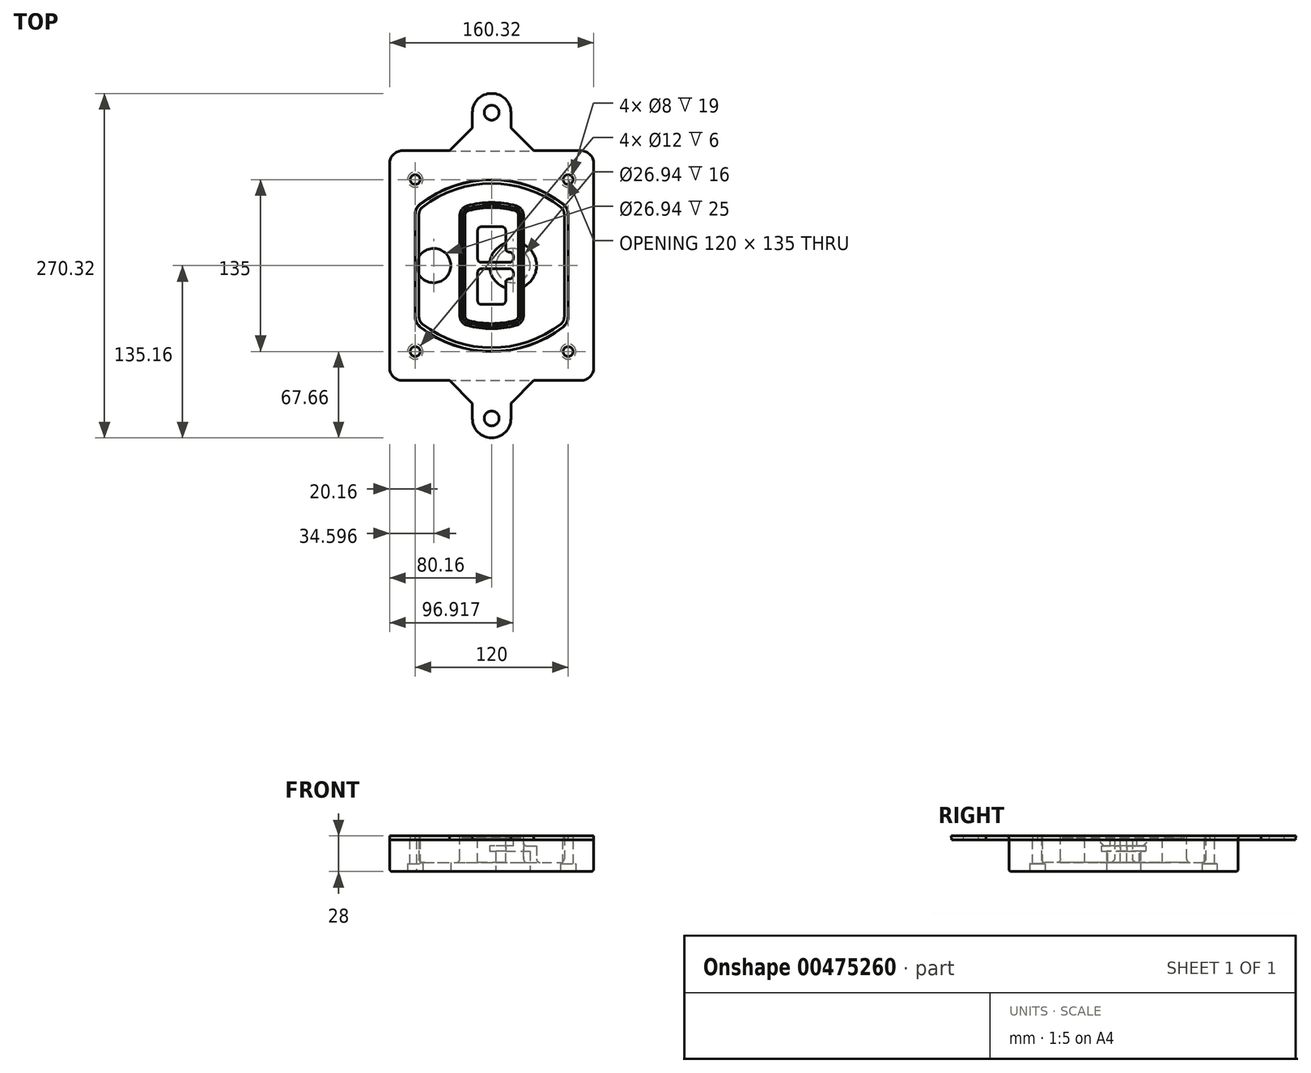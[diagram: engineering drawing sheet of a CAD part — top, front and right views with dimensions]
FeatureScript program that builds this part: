
annotation { "Feature Type Name" : "Feature", "Feature Type Description" : "" }
export const myFeature = defineFeature(function(context is Context, id is Id, definition is map)
    precondition{}
    {
        {
            var Q0;
            Q0=qCreatedBy(makeId("Top.planeOp"),FACE);
            var sketch = newSketch(context, id + "F0", { "sketchPlane" : qUnion([Q0])});
            skPoint(sketch, "E0.rect.middle", {"position": v(0, 0) * mm});
            skLineSegment(sketch, "E1.bottom", {"start": v(-70, -90) * mm, "end": v(70, -90) * mm});
            skLineSegment(sketch, "E1.top", {"start": v(-70, 90) * mm, "end": v(70, 90) * mm});
            skLineSegment(sketch, "E1.left", {"start": v(-80, -80) * mm, "end": v(-80, 80) * mm});
            skLineSegment(sketch, "E1.right", {"start": v(80, -80) * mm, "end": v(80, 80) * mm});
            skLineSegment(sketch, "E2", {"start": v(-80, 90) * mm, "end": v(80, -90) * mm, "construction": true});
            skLineSegment(sketch, "E3", {"start": v(80, 90) * mm, "end": v(-80, -90) * mm, "construction": true});
            skCircle(sketch, "E4", {"center": v(-60, 67.5) * mm, "radius": 4 * mm});
            skCircle(sketch, "E5", {"center": v(60, 67.5) * mm, "radius": 4 * mm});
            skCircle(sketch, "E6", {"center": v(60, -67.5) * mm, "radius": 4 * mm});
            skCircle(sketch, "E7", {"center": v(-60, -67.5) * mm, "radius": 4 * mm});
            skLineSegment(sketch, "E8", {"start": v(-60, 67.5) * mm, "end": v(60, 67.5) * mm, "construction": true});
            skLineSegment(sketch, "E9", {"start": v(60, 67.5) * mm, "end": v(60, -67.5) * mm, "construction": true});
            skLineSegment(sketch, "E10", {"start": v(60, -67.5) * mm, "end": v(-60, -67.5) * mm, "construction": true});
            skLineSegment(sketch, "E11", {"start": v(-60, -67.5) * mm, "end": v(-60, 67.5) * mm, "construction": true});
            skLineSegment(sketch, "E12", {"start": v(-60, 40.3) * mm, "end": v(-60, -40.3) * mm});
            skLineSegment(sketch, "E13", {"start": v(60, 40.3) * mm, "end": v(60, -40.3) * mm});
            skArc(sketch, "E14", {"start": v(56.15, 48.18) * mm, "mid": v(0, 67.5) * mm, "end": v(-56.15, 48.18) * mm});
            skArc(sketch, "E15", {"start": v(-56.15, -48.18) * mm, "mid": v(0, -67.5) * mm, "end": v(56.15, -48.18) * mm});
            skLineSegment(sketch, "E16", {"start": v(-60, 0) * mm, "end": v(60, 0) * mm, "construction": true});
            skPoint(sketch, "E17.visualSharp", {"position": v(-60, -45) * mm});
            skArc(sketch, "E17.filletArc", {"start": v(-60, -40.3) * mm, "mid": v(-58.99, -44.68) * mm, "end": v(-56.15, -48.18) * mm});
            skPoint(sketch, "E18.visualSharp", {"position": v(-60, 45) * mm});
            skArc(sketch, "E18.filletArc", {"start": v(-56.15, 48.18) * mm, "mid": v(-58.99, 44.68) * mm, "end": v(-60, 40.3) * mm});
            skPoint(sketch, "E19.visualSharp", {"position": v(60, 45) * mm});
            skArc(sketch, "E19.filletArc", {"start": v(60, 40.3) * mm, "mid": v(58.99, 44.68) * mm, "end": v(56.15, 48.18) * mm});
            skPoint(sketch, "E20.visualSharp", {"position": v(60, -45) * mm});
            skArc(sketch, "E20.filletArc", {"start": v(56.15, -48.18) * mm, "mid": v(58.99, -44.68) * mm, "end": v(60, -40.3) * mm});
            skPoint(sketch, "E21.visualSharp", {"position": v(-80, 90) * mm});
            skArc(sketch, "E21.filletArc", {"start": v(-70, 90) * mm, "mid": v(-77.07, 87.07) * mm, "end": v(-80, 80) * mm});
            skPoint(sketch, "E22.visualSharp", {"position": v(80, 90) * mm});
            skArc(sketch, "E22.filletArc", {"start": v(80, 80) * mm, "mid": v(77.07, 87.07) * mm, "end": v(70, 90) * mm});
            skPoint(sketch, "E23.visualSharp", {"position": v(80, -90) * mm});
            skArc(sketch, "E23.filletArc", {"start": v(70, -90) * mm, "mid": v(77.07, -87.07) * mm, "end": v(80, -80) * mm});
            skPoint(sketch, "E24.visualSharp", {"position": v(-80, -90) * mm});
            skArc(sketch, "E24.filletArc", {"start": v(-80, -80) * mm, "mid": v(-77.07, -87.07) * mm, "end": v(-70, -90) * mm});
            skArc(sketch, "E25.0", {"start": v(57, 40.3) * mm, "mid": v(56.3, 43.36) * mm, "end": v(54.3, 45.81) * mm});
            skLineSegment(sketch, "E25.1", {"start": v(57, 40.3) * mm, "end": v(57, -40.3) * mm});
            skArc(sketch, "E25.2", {"start": v(54.3, -45.81) * mm, "mid": v(56.3, -43.36) * mm, "end": v(57, -40.3) * mm});
            skArc(sketch, "E25.3", {"start": v(-54.3, -45.81) * mm, "mid": v(0, -64.5) * mm, "end": v(54.3, -45.81) * mm});
            skArc(sketch, "E25.4", {"start": v(-57, -40.3) * mm, "mid": v(-56.3, -43.36) * mm, "end": v(-54.3, -45.81) * mm});
            skArc(sketch, "E25.5", {"start": v(54.3, 45.81) * mm, "mid": v(0, 64.5) * mm, "end": v(-54.3, 45.81) * mm});
            skLineSegment(sketch, "E25.6", {"start": v(-57, 40.3) * mm, "end": v(-57, -40.3) * mm});
            skArc(sketch, "E25.7", {"start": v(-54.3, 45.81) * mm, "mid": v(-56.3, 43.36) * mm, "end": v(-57, 40.3) * mm});
            skArc(sketch, "E26.0", {"start": v(-58.62, 51.33) * mm, "mid": v(-62.58, 46.43) * mm, "end": v(-64, 40.3) * mm});
            skArc(sketch, "E26.1", {"start": v(58.62, 51.33) * mm, "mid": v(0, 71.5) * mm, "end": v(-58.62, 51.33) * mm});
            skArc(sketch, "E26.2", {"start": v(64, 40.3) * mm, "mid": v(62.58, 46.43) * mm, "end": v(58.62, 51.33) * mm});
            skLineSegment(sketch, "E26.3", {"start": v(64, 40.3) * mm, "end": v(64, -40.3) * mm});
            skArc(sketch, "E26.4", {"start": v(58.62, -51.33) * mm, "mid": v(62.58, -46.43) * mm, "end": v(64, -40.3) * mm});
            skLineSegment(sketch, "E26.5", {"start": v(-64, 40.3) * mm, "end": v(-64, -40.3) * mm});
            skArc(sketch, "E26.6", {"start": v(-58.62, -51.33) * mm, "mid": v(0, -71.5) * mm, "end": v(58.62, -51.33) * mm});
            skArc(sketch, "E26.7", {"start": v(-64, -40.3) * mm, "mid": v(-62.58, -46.43) * mm, "end": v(-58.62, -51.33) * mm});
            skSolve(sketch);
        }
        {
            var Q0;
            Q0=makeQuery(id+"F0.imprint","IMPRINT",FACE,{"disambiguationData":[TD([[makeQuery(id+"F0.imprint","IMPRINT",EDGE,{"derivedFrom":sQuery(id+"F0.wireOp",EDGE,"E1.bottom")}),1.0]])]});
            var Q1;
            Q1=makeQuery(id+"F0.imprint","IMPRINT",FACE,{"disambiguationData":[TD([[makeQuery(id+"F0.imprint","IMPRINT",EDGE,{"derivedFrom":sQuery(id+"F0.wireOp",EDGE,"E12")}),1.0]])]});
            var Q2;
            Q2=makeQuery(id+"F0.imprint","IMPRINT",FACE,{"disambiguationData":[TD([[makeQuery(id+"F0.imprint","IMPRINT",EDGE,{"derivedFrom":sQuery(id+"F0.wireOp",EDGE,"E25.0")}),1.0]])]});
            var Q3;
            Q3=makeQuery(id+"F0.imprint","IMPRINT",FACE,{"disambiguationData":[TD([[makeQuery(id+"F0.imprint","IMPRINT",EDGE,{"derivedFrom":sQuery(id+"F0.wireOp",EDGE,"E12")}),-1.0]])]});
            extrude(context, id + "F1", {"entities" : qUnion([Q0, Q1, Q2, Q3]), "oppositeDirection" : true, "depth" : 25 * mm});
        }
        {
            var Q0;
            Q0=makeQuery(id+"F0.imprint","IMPRINT",FACE,{"disambiguationData":[TD([[makeQuery(id+"F0.imprint","IMPRINT",EDGE,{"derivedFrom":sQuery(id+"F0.wireOp",EDGE,"E12")}),1.0]])]});
            extrude(context, id + "F2", {"entities" : qUnion([Q0]), "operationType" : NewBodyOperationType.ADD, "depth" : 3 * mm});
        }
        {
            var Q0;
            Q0=makeQuery(id+"F0.imprint","IMPRINT",FACE,{"disambiguationData":[TD([[makeQuery(id+"F0.imprint","IMPRINT",EDGE,{"derivedFrom":sQuery(id+"F0.wireOp",EDGE,"E25.0")}),1.0]])]});
            extrude(context, id + "F3", {"entities" : qUnion([Q0]), "operationType" : NewBodyOperationType.REMOVE, "oppositeDirection" : true, "depth" : 18 * mm});
        }
        {
            var Q0;
            Q0=makeQuery(id+"F2.opExtrude","CAP_FACE",FACE,{"disambiguationData":[OSD([sQuery(id+"F0.wireOp",EDGE,"E12"),sQuery(id+"F0.wireOp",EDGE,"E13"),sQuery(id+"F0.wireOp",EDGE,"E14"),sQuery(id+"F0.wireOp",EDGE,"E15"),sQuery(id+"F0.wireOp",EDGE,"E17.filletArc"),sQuery(id+"F0.wireOp",EDGE,"E18.filletArc"),sQuery(id+"F0.wireOp",EDGE,"E19.filletArc"),sQuery(id+"F0.wireOp",EDGE,"E20.filletArc"),sQuery(id+"F0.wireOp",EDGE,"E25.0"),sQuery(id+"F0.wireOp",EDGE,"E25.1"),sQuery(id+"F0.wireOp",EDGE,"E25.2"),sQuery(id+"F0.wireOp",EDGE,"E25.3"),sQuery(id+"F0.wireOp",EDGE,"E25.4"),sQuery(id+"F0.wireOp",EDGE,"E25.5"),sQuery(id+"F0.wireOp",EDGE,"E25.6"),sQuery(id+"F0.wireOp",EDGE,"E25.7")])],"isStart":false});
            var sketch = newSketch(context, id + "F4", { "sketchPlane" : qUnion([Q0])});
            skArc(sketch, "E27.0", {"start": v(-19.08, -46.97) * mm, "mid": v(0, -49.5) * mm, "end": v(19.08, -46.97) * mm});
            skArc(sketch, "E28.0", {"start": v(19.08, 46.97) * mm, "mid": v(0, 49.5) * mm, "end": v(-19.08, 46.97) * mm});
            skLineSegment(sketch, "E29", {"start": v(-25, 39.25) * mm, "end": v(-25, -39.25) * mm});
            skLineSegment(sketch, "E30", {"start": v(25, 39.25) * mm, "end": v(25, -39.25) * mm});
            skLineSegment(sketch, "E31", {"start": v(-25, 45.1) * mm, "end": v(25, 45.1) * mm, "construction": true});
            skLineSegment(sketch, "E32", {"start": v(-25, -45.1) * mm, "end": v(25, -45.1) * mm, "construction": true});
            skPoint(sketch, "E33.visualSharp", {"position": v(-25, 45.1) * mm});
            skArc(sketch, "E33.filletArc", {"start": v(-19.08, 46.97) * mm, "mid": v(-23.35, 44.11) * mm, "end": v(-25, 39.25) * mm});
            skPoint(sketch, "E34.visualSharp", {"position": v(25, 45.1) * mm});
            skArc(sketch, "E34.filletArc", {"start": v(25, 39.25) * mm, "mid": v(23.35, 44.11) * mm, "end": v(19.08, 46.97) * mm});
            skPoint(sketch, "E35.visualSharp", {"position": v(25, -45.1) * mm});
            skArc(sketch, "E35.filletArc", {"start": v(19.08, -46.97) * mm, "mid": v(23.35, -44.11) * mm, "end": v(25, -39.25) * mm});
            skPoint(sketch, "E36.visualSharp", {"position": v(-25, -45.1) * mm});
            skArc(sketch, "E36.filletArc", {"start": v(-25, -39.25) * mm, "mid": v(-23.35, -44.11) * mm, "end": v(-19.08, -46.97) * mm});
            skArc(sketch, "E37.0", {"start": v(54.3, 45.81) * mm, "mid": v(0, 64.5) * mm, "end": v(-54.3, 45.81) * mm});
            skArc(sketch, "E37.1", {"start": v(-54.3, 45.81) * mm, "mid": v(-56.3, 43.36) * mm, "end": v(-57, 40.3) * mm});
            skLineSegment(sketch, "E37.2", {"start": v(-57, 40.3) * mm, "end": v(-57, -40.3) * mm});
            skArc(sketch, "E37.3", {"start": v(-57, -40.3) * mm, "mid": v(-56.3, -43.36) * mm, "end": v(-54.3, -45.81) * mm});
            skArc(sketch, "E37.4", {"start": v(-54.3, -45.81) * mm, "mid": v(0, -64.5) * mm, "end": v(54.3, -45.81) * mm});
            skArc(sketch, "E37.5", {"start": v(54.3, -45.81) * mm, "mid": v(56.3, -43.36) * mm, "end": v(57, -40.3) * mm});
            skLineSegment(sketch, "E37.6", {"start": v(57, 40.3) * mm, "end": v(57, -40.3) * mm});
            skArc(sketch, "E37.7", {"start": v(57, 40.3) * mm, "mid": v(56.3, 43.36) * mm, "end": v(54.3, 45.81) * mm});
            skLineSegment(sketch, "E38.0", {"start": v(23, 39.25) * mm, "end": v(23, -39.25) * mm});
            skArc(sketch, "E38.1", {"start": v(18.56, -45.04) * mm, "mid": v(21.76, -42.9) * mm, "end": v(23, -39.25) * mm});
            skArc(sketch, "E38.2", {"start": v(-18.56, -45.04) * mm, "mid": v(0, -47.5) * mm, "end": v(18.56, -45.04) * mm});
            skArc(sketch, "E38.3", {"start": v(-23, -39.25) * mm, "mid": v(-21.76, -42.9) * mm, "end": v(-18.56, -45.04) * mm});
            skLineSegment(sketch, "E38.4", {"start": v(-23, 39.25) * mm, "end": v(-23, -39.25) * mm});
            skArc(sketch, "E38.5", {"start": v(23, 39.25) * mm, "mid": v(21.76, 42.9) * mm, "end": v(18.56, 45.04) * mm});
            skArc(sketch, "E38.6", {"start": v(-18.56, 45.04) * mm, "mid": v(-21.76, 42.9) * mm, "end": v(-23, 39.25) * mm});
            skArc(sketch, "E38.7", {"start": v(18.56, 45.04) * mm, "mid": v(0, 47.5) * mm, "end": v(-18.56, 45.04) * mm});
            skArc(sketch, "E39.0", {"start": v(21, 39.25) * mm, "mid": v(20.18, 41.68) * mm, "end": v(18.04, 43.1) * mm});
            skLineSegment(sketch, "E39.1", {"start": v(21, 39.25) * mm, "end": v(21, -39.25) * mm});
            skArc(sketch, "E39.2", {"start": v(18.04, -43.1) * mm, "mid": v(20.18, -41.68) * mm, "end": v(21, -39.25) * mm});
            skArc(sketch, "E39.3", {"start": v(-18.04, -43.1) * mm, "mid": v(0, -45.5) * mm, "end": v(18.04, -43.1) * mm});
            skArc(sketch, "E39.4", {"start": v(-21, -39.25) * mm, "mid": v(-20.18, -41.68) * mm, "end": v(-18.04, -43.1) * mm});
            skArc(sketch, "E39.5", {"start": v(18.04, 43.1) * mm, "mid": v(0, 45.5) * mm, "end": v(-18.04, 43.1) * mm});
            skLineSegment(sketch, "E39.6", {"start": v(-21, 39.25) * mm, "end": v(-21, -39.25) * mm});
            skArc(sketch, "E39.7", {"start": v(-18.04, 43.1) * mm, "mid": v(-20.18, 41.68) * mm, "end": v(-21, 39.25) * mm});
            skLineSegment(sketch, "E40", {"start": v(-25, 0) * mm, "end": v(25, 0) * mm, "construction": true});
            skLineSegment(sketch, "E41", {"start": v(-11, 5.5) * mm, "end": v(-11, 27.5) * mm});
            skLineSegment(sketch, "E42", {"start": v(-8, 30.5) * mm, "end": v(8, 30.5) * mm});
            skLineSegment(sketch, "E43", {"start": v(11, 27.5) * mm, "end": v(11, 13.5) * mm});
            skLineSegment(sketch, "E44", {"start": v(14, 10.5) * mm, "end": v(14, 10.5) * mm});
            skLineSegment(sketch, "E45", {"start": v(17, 7.5) * mm, "end": v(17, 5.5) * mm});
            skLineSegment(sketch, "E46", {"start": v(14, 2.5) * mm, "end": v(-8, 2.5) * mm});
            skPoint(sketch, "E47.visualSharp", {"position": v(-11, 30.5) * mm});
            skArc(sketch, "E47.filletArc", {"start": v(-8, 30.5) * mm, "mid": v(-10.12, 29.62) * mm, "end": v(-11, 27.5) * mm});
            skPoint(sketch, "E48.visualSharp", {"position": v(11, 30.5) * mm});
            skArc(sketch, "E48.filletArc", {"start": v(11, 27.5) * mm, "mid": v(10.12, 29.62) * mm, "end": v(8, 30.5) * mm});
            skPoint(sketch, "E49.visualSharp", {"position": v(11, 10.5) * mm});
            skArc(sketch, "E49.filletArc", {"start": v(11, 13.5) * mm, "mid": v(11.88, 11.38) * mm, "end": v(14, 10.5) * mm});
            skPoint(sketch, "E50.visualSharp", {"position": v(17, 10.5) * mm});
            skArc(sketch, "E50.filletArc", {"start": v(17, 7.5) * mm, "mid": v(16.12, 9.62) * mm, "end": v(14, 10.5) * mm});
            skPoint(sketch, "E51.visualSharp", {"position": v(17, 2.5) * mm});
            skArc(sketch, "E51.filletArc", {"start": v(14, 2.5) * mm, "mid": v(16.12, 3.38) * mm, "end": v(17, 5.5) * mm});
            skPoint(sketch, "E52.visualSharp", {"position": v(-11, 2.5) * mm});
            skArc(sketch, "E52.filletArc", {"start": v(-11, 5.5) * mm, "mid": v(-10.12, 3.38) * mm, "end": v(-8, 2.5) * mm});
            skLineSegment(sketch, "E53.0.MirrorCS", {"start": v(14, -2.5) * mm, "end": v(-8, -2.5) * mm});
            skArc(sketch, "E54.0.MirrorCS", {"start": v(-11, -5.5) * mm, "mid": v(-10.12, -3.38) * mm, "end": v(-8, -2.5) * mm});
            skLineSegment(sketch, "E55.0.MirrorCS", {"start": v(-11, -5.5) * mm, "end": v(-11, -27.5) * mm});
            skArc(sketch, "E56.0.MirrorCS", {"start": v(-8, -30.5) * mm, "mid": v(-10.12, -29.62) * mm, "end": v(-11, -27.5) * mm});
            skLineSegment(sketch, "E57.0.MirrorCS", {"start": v(-8, -30.5) * mm, "end": v(8, -30.5) * mm});
            skArc(sketch, "E58.0.MirrorCS", {"start": v(11, -27.5) * mm, "mid": v(10.12, -29.62) * mm, "end": v(8, -30.5) * mm});
            skLineSegment(sketch, "E59.0.MirrorCS", {"start": v(11, -27.5) * mm, "end": v(11, -13.5) * mm});
            skArc(sketch, "E60.0.MirrorCS", {"start": v(11, -13.5) * mm, "mid": v(11.88, -11.38) * mm, "end": v(14, -10.5) * mm});
            skArc(sketch, "E61.0.MirrorCS", {"start": v(17, -7.5) * mm, "mid": v(16.12, -9.62) * mm, "end": v(14, -10.5) * mm});
            skLineSegment(sketch, "E62.0.MirrorCS", {"start": v(17, -7.5) * mm, "end": v(17, -5.5) * mm});
            skArc(sketch, "E63.0.MirrorCS", {"start": v(14, -2.5) * mm, "mid": v(16.12, -3.38) * mm, "end": v(17, -5.5) * mm});
            skSolve(sketch);
        }
        {
            var Q0;
            Q0=makeQuery(id+"F4.imprint","IMPRINT",FACE,{"disambiguationData":[TD([[makeQuery(id+"F4.imprint","IMPRINT",EDGE,{"derivedFrom":sQuery(id+"F4.wireOp",EDGE,"E27.0")}),1.0]])]});
            var Q1;
            Q1=makeQuery(id+"F4.imprint","IMPRINT",FACE,{"disambiguationData":[TD([[makeQuery(id+"F4.imprint","IMPRINT",EDGE,{"derivedFrom":sQuery(id+"F4.wireOp",EDGE,"E38.0")}),-1.0]])]});
            var Q2;
            Q2=makeQuery(id+"F4.imprint","IMPRINT",FACE,{"disambiguationData":[TD([[makeQuery(id+"F4.imprint","IMPRINT",EDGE,{"derivedFrom":sQuery(id+"F4.wireOp",EDGE,"E39.0")}),1.0]])]});
            extrude(context, id + "F5", {"entities" : qUnion([Q0, Q1, Q2]), "operationType" : NewBodyOperationType.ADD, "endBound" : BoundingType.UP_TO_NEXT, "oppositeDirection" : true, "depth" : 25 * mm});
        }
        {
            var Q0;
            Q0=makeQuery(id+"F4.imprint","IMPRINT",FACE,{"disambiguationData":[TD([[makeQuery(id+"F4.imprint","IMPRINT",EDGE,{"derivedFrom":sQuery(id+"F4.wireOp",EDGE,"E38.0")}),-1.0]])]});
            extrude(context, id + "F6", {"entities" : qUnion([Q0]), "operationType" : NewBodyOperationType.REMOVE, "oppositeDirection" : true, "depth" : 2 * mm});
        }
        {
            var Q0;
            Q0=makeQuery(id+"F1.opExtrude","CAP_FACE",FACE,{"disambiguationData":[OSD([sQuery(id+"F0.wireOp",EDGE,"E1.bottom"),sQuery(id+"F0.wireOp",EDGE,"E1.top"),sQuery(id+"F0.wireOp",EDGE,"E1.left"),sQuery(id+"F0.wireOp",EDGE,"E1.right"),sQuery(id+"F0.wireOp",EDGE,"E4"),sQuery(id+"F0.wireOp",EDGE,"E5"),sQuery(id+"F0.wireOp",EDGE,"E6"),sQuery(id+"F0.wireOp",EDGE,"E7"),sQuery(id+"F0.wireOp",EDGE,"E21.filletArc"),sQuery(id+"F0.wireOp",EDGE,"E22.filletArc"),sQuery(id+"F0.wireOp",EDGE,"E23.filletArc"),sQuery(id+"F0.wireOp",EDGE,"E24.filletArc")])],"isStart":false});
            var sketch = newSketch(context, id + "F7", { "sketchPlane" : qUnion([Q0])});
            skCircle(sketch, "E64", {"center": v(16.76, 0) * mm, "radius": 13.47 * mm});
            skCircle(sketch, "E65", {"center": v(-45.56, 0) * mm, "radius": 13.47 * mm});
            skLineSegment(sketch, "E66", {"start": v(80, 0) * mm, "end": v(-80, 0) * mm});
            skCircle(sketch, "E67", {"center": v(16.76, 0) * mm, "radius": 18.47 * mm});
            skCircle(sketch, "E68", {"center": v(60, -67.5) * mm, "radius": 6 * mm});
            skCircle(sketch, "E69", {"center": v(-60, -67.5) * mm, "radius": 6 * mm});
            skCircle(sketch, "E70", {"center": v(-60, 67.5) * mm, "radius": 6 * mm});
            skCircle(sketch, "E71", {"center": v(60, 67.5) * mm, "radius": 6 * mm});
            skSolve(sketch);
        }
        {
            var Q0;
            {var subQ1=sQuery(id+"F7.wireOp",EDGE,"E66");var subQ4=sQuery(id+"F7.wireOp",EDGE,"E64");var subQ6=makeQuery(id+"F7.imprint","INTERSECT",VERTEX,{"disambiguationData":[OD(0.0)],"derivedFrom":[subQ4,subQ1]});Q0=makeQuery(id+"F7.imprint","IMPRINT",FACE,{"disambiguationData":[TD([[makeQuery(id+"F7.imprint","IMPRINT",EDGE,{"disambiguationData":[TD([[subQ6,-1.0]])],"derivedFrom":subQ4}),-1.0]])]});}
            var Q1;
            {var subQ0=sQuery(id+"F7.wireOp",EDGE,"E66");var subQ1=sQuery(id+"F7.wireOp",EDGE,"E64");var subQ3=makeQuery(id+"F7.imprint","INTERSECT",VERTEX,{"disambiguationData":[OD(0.0)],"derivedFrom":[subQ1,subQ0]});Q1=makeQuery(id+"F7.imprint","IMPRINT",FACE,{"disambiguationData":[TD([[makeQuery(id+"F7.imprint","IMPRINT",EDGE,{"disambiguationData":[TD([[subQ3,-1.0]])],"derivedFrom":subQ1}),1.0]])]});}
            var Q2;
            {var subQ0=sQuery(id+"F7.wireOp",EDGE,"E66");var subQ1=sQuery(id+"F7.wireOp",EDGE,"E64");var subQ3=makeQuery(id+"F7.imprint","INTERSECT",VERTEX,{"disambiguationData":[OD(0.0)],"derivedFrom":[subQ1,subQ0]});Q2=makeQuery(id+"F7.imprint","IMPRINT",FACE,{"disambiguationData":[TD([[makeQuery(id+"F7.imprint","IMPRINT",EDGE,{"disambiguationData":[TD([[subQ3,1.0]])],"derivedFrom":subQ1}),1.0]])]});}
            var Q3;
            {var subQ1=sQuery(id+"F7.wireOp",EDGE,"E66");var subQ4=sQuery(id+"F7.wireOp",EDGE,"E64");var subQ6=makeQuery(id+"F7.imprint","INTERSECT",VERTEX,{"disambiguationData":[OD(0.0)],"derivedFrom":[subQ4,subQ1]});Q3=makeQuery(id+"F7.imprint","IMPRINT",FACE,{"disambiguationData":[TD([[makeQuery(id+"F7.imprint","IMPRINT",EDGE,{"disambiguationData":[TD([[subQ6,1.0]])],"derivedFrom":subQ4}),-1.0]])]});}
            extrude(context, id + "F8", {"entities" : qUnion([Q0, Q1, Q2, Q3]), "operationType" : NewBodyOperationType.ADD, "oppositeDirection" : true, "depth" : 20 * mm});
        }
        {
            var Q0;
            {var subQ0=sQuery(id+"F7.wireOp",EDGE,"E66");var subQ1=sQuery(id+"F7.wireOp",EDGE,"E64");var subQ3=makeQuery(id+"F7.imprint","INTERSECT",VERTEX,{"disambiguationData":[OD(0.0)],"derivedFrom":[subQ1,subQ0]});Q0=makeQuery(id+"F7.imprint","IMPRINT",FACE,{"disambiguationData":[TD([[makeQuery(id+"F7.imprint","IMPRINT",EDGE,{"disambiguationData":[TD([[subQ3,-1.0]])],"derivedFrom":subQ1}),1.0]])]});}
            var Q1;
            {var subQ0=sQuery(id+"F7.wireOp",EDGE,"E66");var subQ1=sQuery(id+"F7.wireOp",EDGE,"E64");var subQ3=makeQuery(id+"F7.imprint","INTERSECT",VERTEX,{"disambiguationData":[OD(0.0)],"derivedFrom":[subQ1,subQ0]});Q1=makeQuery(id+"F7.imprint","IMPRINT",FACE,{"disambiguationData":[TD([[makeQuery(id+"F7.imprint","IMPRINT",EDGE,{"disambiguationData":[TD([[subQ3,1.0]])],"derivedFrom":subQ1}),1.0]])]});}
            extrude(context, id + "F9", {"entities" : qUnion([Q0, Q1]), "operationType" : NewBodyOperationType.REMOVE, "oppositeDirection" : true, "depth" : 16 * mm});
        }
        {
            var Q0;
            {var subQ0=sQuery(id+"F7.wireOp",EDGE,"E66");var subQ1=sQuery(id+"F7.wireOp",EDGE,"E65");var subQ3=makeQuery(id+"F7.imprint","INTERSECT",VERTEX,{"disambiguationData":[OD(0.0)],"derivedFrom":[subQ1,subQ0]});Q0=makeQuery(id+"F7.imprint","IMPRINT",FACE,{"disambiguationData":[TD([[makeQuery(id+"F7.imprint","IMPRINT",EDGE,{"disambiguationData":[TD([[subQ3,-1.0]])],"derivedFrom":subQ1}),1.0]])]});}
            var Q1;
            {var subQ0=sQuery(id+"F7.wireOp",EDGE,"E66");var subQ1=sQuery(id+"F7.wireOp",EDGE,"E65");var subQ3=makeQuery(id+"F7.imprint","INTERSECT",VERTEX,{"disambiguationData":[OD(0.0)],"derivedFrom":[subQ1,subQ0]});Q1=makeQuery(id+"F7.imprint","IMPRINT",FACE,{"disambiguationData":[TD([[makeQuery(id+"F7.imprint","IMPRINT",EDGE,{"disambiguationData":[TD([[subQ3,1.0]])],"derivedFrom":subQ1}),1.0]])]});}
            extrude(context, id + "F10", {"entities" : qUnion([Q0, Q1]), "operationType" : NewBodyOperationType.REMOVE, "oppositeDirection" : true, "depth" : 25 * mm});
        }
        {
            var Q0;
            Q0=makeQuery(id+"F7.imprint","IMPRINT",FACE,{"disambiguationData":[TD([[makeQuery(id+"F7.imprint","IMPRINT",EDGE,{"derivedFrom":sQuery(id+"F7.wireOp",EDGE,"E68")}),1.0]])]});
            var Q1;
            Q1=makeQuery(id+"F7.imprint","IMPRINT",FACE,{"disambiguationData":[TD([[makeQuery(id+"F7.imprint","IMPRINT",EDGE,{"derivedFrom":makeQuery(id+"F1.opExtrude","CAP_EDGE",EDGE,{"disambiguationData":[OSD([sQuery(id+"F0.wireOp",EDGE,"E5")])],"isStart":false})}),-1.0]])]});
            var Q2;
            Q2=makeQuery(id+"F7.imprint","IMPRINT",FACE,{"disambiguationData":[TD([[makeQuery(id+"F7.imprint","IMPRINT",EDGE,{"derivedFrom":sQuery(id+"F7.wireOp",EDGE,"E69")}),1.0]])]});
            var Q3;
            Q3=makeQuery(id+"F7.imprint","IMPRINT",FACE,{"disambiguationData":[TD([[makeQuery(id+"F7.imprint","IMPRINT",EDGE,{"derivedFrom":makeQuery(id+"F1.opExtrude","CAP_EDGE",EDGE,{"disambiguationData":[OSD([sQuery(id+"F0.wireOp",EDGE,"E4")])],"isStart":false})}),-1.0]])]});
            var Q4;
            Q4=makeQuery(id+"F7.imprint","IMPRINT",FACE,{"disambiguationData":[TD([[makeQuery(id+"F7.imprint","IMPRINT",EDGE,{"derivedFrom":sQuery(id+"F7.wireOp",EDGE,"E70")}),1.0]])]});
            var Q5;
            Q5=makeQuery(id+"F7.imprint","IMPRINT",FACE,{"disambiguationData":[TD([[makeQuery(id+"F7.imprint","IMPRINT",EDGE,{"derivedFrom":makeQuery(id+"F1.opExtrude","CAP_EDGE",EDGE,{"disambiguationData":[OSD([sQuery(id+"F0.wireOp",EDGE,"E7")])],"isStart":false})}),-1.0]])]});
            var Q6;
            Q6=makeQuery(id+"F7.imprint","IMPRINT",FACE,{"disambiguationData":[TD([[makeQuery(id+"F7.imprint","IMPRINT",EDGE,{"derivedFrom":sQuery(id+"F7.wireOp",EDGE,"E71")}),1.0]])]});
            var Q7;
            Q7=makeQuery(id+"F7.imprint","IMPRINT",FACE,{"disambiguationData":[TD([[makeQuery(id+"F7.imprint","IMPRINT",EDGE,{"derivedFrom":makeQuery(id+"F1.opExtrude","CAP_EDGE",EDGE,{"disambiguationData":[OSD([sQuery(id+"F0.wireOp",EDGE,"E6")])],"isStart":false})}),-1.0]])]});
            extrude(context, id + "F11", {"entities" : qUnion([Q0, Q1, Q2, Q3, Q4, Q5, Q6, Q7]), "operationType" : NewBodyOperationType.REMOVE, "oppositeDirection" : true, "depth" : 6 * mm});
        }
        {
            var Q0;
            Q0=makeQuery(id+"F9.boolean.opBoolean","COPY",FACE,{"derivedFrom":makeQuery(id+"F9.opExtrude","CAP_FACE",FACE,{"disambiguationData":[OSD([sQuery(id+"F7.wireOp",EDGE,"E64")])],"isStart":false})});
            var sketch = newSketch(context, id + "F12", { "sketchPlane" : qUnion([Q0])});
            skArc(sketch, "E72.0", {"start": v(11, 17.55) * mm, "mid": v(2.57, 11.82) * mm, "end": v(-1.54, 2.5) * mm});
            skArc(sketch, "E72.1", {"start": v(-1.54, -2.5) * mm, "mid": v(2.57, -11.82) * mm, "end": v(11, -17.55) * mm});
            skLineSegment(sketch, "E73", {"start": v(-1.54, -2.5) * mm, "end": v(14, -2.5) * mm});
            skLineSegment(sketch, "E74.0", {"start": v(14, 2.5) * mm, "end": v(-1.54, 2.5) * mm});
            skArc(sketch, "E74.1", {"start": v(14, 2.5) * mm, "mid": v(16.12, 3.38) * mm, "end": v(17, 5.5) * mm});
            skLineSegment(sketch, "E74.2", {"start": v(17, 7.5) * mm, "end": v(17, 5.5) * mm});
            skArc(sketch, "E74.3", {"start": v(17, 7.5) * mm, "mid": v(16.12, 9.62) * mm, "end": v(14, 10.5) * mm});
            skArc(sketch, "E74.4", {"start": v(11, 13.5) * mm, "mid": v(11.88, 11.38) * mm, "end": v(14, 10.5) * mm});
            skLineSegment(sketch, "E74.5", {"start": v(11, 17.55) * mm, "end": v(11, 13.5) * mm});
            skLineSegment(sketch, "E74.7", {"start": v(14, -2.5) * mm, "end": v(-1.54, -2.5) * mm});
            skArc(sketch, "E74.8", {"start": v(14, -2.5) * mm, "mid": v(16.12, -3.38) * mm, "end": v(17, -5.5) * mm});
            skLineSegment(sketch, "E74.9", {"start": v(17, -7.5) * mm, "end": v(17, -5.5) * mm});
            skArc(sketch, "E74.10", {"start": v(17, -7.5) * mm, "mid": v(16.12, -9.62) * mm, "end": v(14, -10.5) * mm});
            skArc(sketch, "E74.11", {"start": v(11, -13.5) * mm, "mid": v(11.88, -11.38) * mm, "end": v(14, -10.5) * mm});
            skLineSegment(sketch, "E74.12", {"start": v(11, -17.55) * mm, "end": v(11, -13.5) * mm});
            skPoint(sketch, "E75.orphan", {"position": v(11, -27.5) * mm});
            skPoint(sketch, "E76.orphan", {"position": v(-8, -2.5) * mm});
            skPoint(sketch, "E77.orphan", {"position": v(-8, 2.5) * mm});
            skPoint(sketch, "E78.orphan", {"position": v(11, 27.5) * mm});
            skSolve(sketch);
        }
        {
            var Q0;
            {var subQ7=sQuery(id+"F12.wireOp",EDGE,"E72.0");var subQ14=sQuery(id+"F12.wireOp",EDGE,"E72.1");var subQ16=sQuery(id+"F12.wireOp",EDGE,"E74.1");var subQ18=sQuery(id+"F12.wireOp",EDGE,"E74.8");Q0=qUnion([makeQuery(id+"F12.imprint","IMPRINT",FACE,{"disambiguationData":[TD([[makeQuery(id+"F12.imprint","IMPRINT",EDGE,{"derivedFrom":subQ7}),1.0]])]}),makeQuery(id+"F12.imprint","IMPRINT",FACE,{"disambiguationData":[TD([[makeQuery(id+"F12.imprint","IMPRINT",EDGE,{"derivedFrom":subQ14}),1.0]])]}),makeQuery(id+"F12.imprint","IMPRINT",FACE,{"disambiguationData":[TD([[makeQuery(id+"F12.imprint","IMPRINT",EDGE,{"derivedFrom":subQ16}),1.0]])]}),makeQuery(id+"F12.imprint","IMPRINT",FACE,{"disambiguationData":[TD([[makeQuery(id+"F12.imprint","IMPRINT",EDGE,{"derivedFrom":subQ18}),-1.0]])]})]);}
            var Q1;
            Q1=makeQuery(id+"F5.boolean.opBoolean","SPLIT",FACE,{"disambiguationData":[TD([makeQuery(id+"F5.opExtrude","SWEPT_FACE",FACE,{"disambiguationData":[OSD([sQuery(id+"F4.wireOp",EDGE,"E41")])]})])],"derivedFrom":makeQuery(id+"F3.boolean.opBoolean","COPY",FACE,{"derivedFrom":makeQuery(id+"F3.opExtrude","CAP_FACE",FACE,{"disambiguationData":[OSD([sQuery(id+"F0.wireOp",EDGE,"E25.0"),sQuery(id+"F0.wireOp",EDGE,"E25.1"),sQuery(id+"F0.wireOp",EDGE,"E25.2"),sQuery(id+"F0.wireOp",EDGE,"E25.3"),sQuery(id+"F0.wireOp",EDGE,"E25.4"),sQuery(id+"F0.wireOp",EDGE,"E25.5"),sQuery(id+"F0.wireOp",EDGE,"E25.6"),sQuery(id+"F0.wireOp",EDGE,"E25.7")])],"isStart":false})})});
            extrude(context, id + "F13", {"entities" : qUnion([Q0]), "operationType" : NewBodyOperationType.REMOVE, "endBound" : BoundingType.UP_TO_SURFACE, "endBoundEntityFace" : qUnion([Q1]), "depth" : 25 * mm});
        }
        {
            var Q0;
            Q0=makeQuery(id+"F3.boolean.opBoolean","COPY",EDGE,{"derivedFrom":makeQuery(id+"F3.opExtrude","CAP_EDGE",EDGE,{"disambiguationData":[OSD([sQuery(id+"F0.wireOp",EDGE,"E25.6")])],"isStart":false})});
            var Q1;
            Q1=makeQuery(id+"F8.boolean.opBoolean","INTERSECT",EDGE,{"derivedFrom":[makeQuery(id+"F5.opExtrude","SWEPT_FACE",FACE,{"disambiguationData":[OSD([sQuery(id+"F4.wireOp",EDGE,"E30")])]}),makeQuery(id+"F8.opExtrude","CAP_FACE",FACE,{"disambiguationData":[OSD([sQuery(id+"F7.wireOp",EDGE,"E67")])],"isStart":false})]});
            var Q2;
            Q2=makeQuery(id+"F8.boolean.opBoolean","INTERSECT",EDGE,{"disambiguationData":[OD(1.0)],"derivedFrom":[makeQuery(id+"F5.opExtrude","SWEPT_FACE",FACE,{"disambiguationData":[OSD([sQuery(id+"F4.wireOp",EDGE,"E30")])]}),makeQuery(id+"F8.opExtrude","SWEPT_FACE",FACE,{"disambiguationData":[OSD([sQuery(id+"F7.wireOp",EDGE,"E67")])]})]});
            var Q3;
            {var subQ0=sQuery(id+"F4.wireOp",EDGE,"E30");Q3=makeQuery(id+"F8.boolean.opBoolean","SPLIT",EDGE,{"disambiguationData":[TD([makeQuery(id+"F5.opExtrude","SWEPT_FACE",FACE,{"disambiguationData":[OSD([sQuery(id+"F4.wireOp",EDGE,"E35.filletArc")])]})])],"derivedFrom":makeQuery(id+"F5.opExtrude","CAP_EDGE",EDGE,{"disambiguationData":[OSD([subQ0])],"isStart":false})});}
            var Q4;
            {var subQ0=sQuery(id+"F0.wireOp",EDGE,"E25.7");var subQ1=sQuery(id+"F0.wireOp",EDGE,"E25.1");var subQ2=sQuery(id+"F0.wireOp",EDGE,"E25.6");var subQ3=sQuery(id+"F0.wireOp",EDGE,"E25.5");var subQ4=sQuery(id+"F0.wireOp",EDGE,"E25.4");var subQ5=sQuery(id+"F0.wireOp",EDGE,"E25.0");var subQ6=sQuery(id+"F0.wireOp",EDGE,"E25.2");var subQ7=sQuery(id+"F0.wireOp",EDGE,"E25.3");Q4=makeQuery(id+"F8.boolean.opBoolean","INTERSECT",EDGE,{"derivedFrom":[makeQuery(id+"F5.boolean.opBoolean","SPLIT",FACE,{"disambiguationData":[TD([makeQuery(id+"F2.opExtrude","SWEPT_FACE",FACE,{"disambiguationData":[OSD([subQ5])]})])],"derivedFrom":makeQuery(id+"F3.boolean.opBoolean","COPY",FACE,{"derivedFrom":makeQuery(id+"F3.opExtrude","CAP_FACE",FACE,{"disambiguationData":[OSD([subQ5,subQ1,subQ6,subQ7,subQ4,subQ3,subQ2,subQ0])],"isStart":false})})}),makeQuery(id+"F8.opExtrude","SWEPT_FACE",FACE,{"disambiguationData":[OSD([sQuery(id+"F7.wireOp",EDGE,"E67")])]})]});}
            var Q5;
            Q5=makeQuery(id+"F8.boolean.opBoolean","INTERSECT",EDGE,{"disambiguationData":[OD(0.0)],"derivedFrom":[makeQuery(id+"F5.opExtrude","SWEPT_FACE",FACE,{"disambiguationData":[OSD([sQuery(id+"F4.wireOp",EDGE,"E30")])]}),makeQuery(id+"F8.opExtrude","SWEPT_FACE",FACE,{"disambiguationData":[OSD([sQuery(id+"F7.wireOp",EDGE,"E67")])]})]});
            fillet(context, id + "F14", {"entities" : qUnion([Q0, Q1, Q2, Q3, Q4, Q5]), "radius" : 3 * mm, "tangentPropagation" : true, "allowEdgeOverflow" : false});
        }
        {
            var Q0;
            Q0=makeQuery(id+"F1.opExtrude","CAP_EDGE",EDGE,{"disambiguationData":[OSD([sQuery(id+"F0.wireOp",EDGE,"E1.bottom")])],"isStart":false});
            fillet(context, id + "F15", {"entities" : qUnion([Q0]), "radius" : 2 * mm, "tangentPropagation" : true, "allowEdgeOverflow" : false});
        }
        {
            var Q0;
            {var subQ0=sQuery(id+"F0.wireOp",EDGE,"E21.filletArc");var subQ1=sQuery(id+"F0.wireOp",EDGE,"E7");var subQ2=sQuery(id+"F0.wireOp",EDGE,"E6");var subQ3=sQuery(id+"F0.wireOp",EDGE,"E5");var subQ4=sQuery(id+"F0.wireOp",EDGE,"E4");var subQ5=sQuery(id+"F0.wireOp",EDGE,"E22.filletArc");var subQ6=sQuery(id+"F0.wireOp",EDGE,"E1.bottom");var subQ7=sQuery(id+"F0.wireOp",EDGE,"E1.right");var subQ8=sQuery(id+"F0.wireOp",EDGE,"E1.top");var subQ9=sQuery(id+"F0.wireOp",EDGE,"E1.left");var subQ10=sQuery(id+"F0.wireOp",EDGE,"E23.filletArc");var subQ11=sQuery(id+"F0.wireOp",EDGE,"E24.filletArc");Q0=makeQuery(id+"F2.boolean.opBoolean","SPLIT",FACE,{"disambiguationData":[TD([makeQuery(id+"F1.opExtrude","SWEPT_FACE",FACE,{"disambiguationData":[OSD([subQ6])]})])],"derivedFrom":makeQuery(id+"F1.opExtrude","CAP_FACE",FACE,{"disambiguationData":[OSD([subQ6,subQ8,subQ9,subQ7,subQ4,subQ3,subQ2,subQ1,subQ0,subQ5,subQ10,subQ11])],"isStart":true})});}
            var sketch = newSketch(context, id + "F16", { "sketchPlane" : qUnion([Q0])});
            skLineSegment(sketch, "E79.0", {"start": v(-70, 90) * mm, "end": v(70, 90) * mm});
            skArc(sketch, "E79.1", {"start": v(-70, 90) * mm, "mid": v(-77.07, 87.07) * mm, "end": v(-80, 80) * mm});
            skLineSegment(sketch, "E79.2", {"start": v(-80, -80) * mm, "end": v(-80, 80) * mm});
            skArc(sketch, "E79.3", {"start": v(-80, -80) * mm, "mid": v(-77.07, -87.07) * mm, "end": v(-70, -90) * mm});
            skLineSegment(sketch, "E79.4", {"start": v(-70, -90) * mm, "end": v(70, -90) * mm});
            skArc(sketch, "E79.5", {"start": v(70, -90) * mm, "mid": v(77.07, -87.07) * mm, "end": v(80, -80) * mm});
            skLineSegment(sketch, "E79.6", {"start": v(80, -80) * mm, "end": v(80, 80) * mm});
            skArc(sketch, "E79.7", {"start": v(80, 80) * mm, "mid": v(77.07, 87.07) * mm, "end": v(70, 90) * mm});
            skArc(sketch, "E79.8", {"start": v(56.15, 48.18) * mm, "mid": v(0, 67.5) * mm, "end": v(-56.15, 48.18) * mm});
            skArc(sketch, "E79.9", {"start": v(-56.15, 48.18) * mm, "mid": v(-58.99, 44.68) * mm, "end": v(-60, 40.3) * mm});
            skLineSegment(sketch, "E79.10", {"start": v(-60, 40.3) * mm, "end": v(-60, -40.3) * mm});
            skArc(sketch, "E79.11", {"start": v(-60, -40.3) * mm, "mid": v(-58.99, -44.68) * mm, "end": v(-56.15, -48.18) * mm});
            skArc(sketch, "E79.12", {"start": v(-56.15, -48.18) * mm, "mid": v(0, -67.5) * mm, "end": v(56.15, -48.18) * mm});
            skLineSegment(sketch, "E79.13", {"start": v(60, 40.3) * mm, "end": v(60, -40.3) * mm});
            skArc(sketch, "E79.14", {"start": v(56.15, -48.18) * mm, "mid": v(58.99, -44.68) * mm, "end": v(60, -40.3) * mm});
            skArc(sketch, "E79.15", {"start": v(60, 40.3) * mm, "mid": v(58.99, 44.68) * mm, "end": v(56.15, 48.18) * mm});
            skLineSegment(sketch, "E80", {"start": v(0, 90) * mm, "end": v(0, 120) * mm, "construction": true});
            skArc(sketch, "E81", {"start": v(15, 120) * mm, "mid": v(0, 135) * mm, "end": v(-15, 120) * mm});
            skLineSegment(sketch, "E82", {"start": v(-15, 120) * mm, "end": v(-15, 108) * mm});
            skLineSegment(sketch, "E83", {"start": v(-15, 108) * mm, "end": v(-33, 90) * mm});
            skCircle(sketch, "E84", {"center": v(0, 120) * mm, "radius": 6 * mm});
            skLineSegment(sketch, "E85", {"start": v(-80, 0) * mm, "end": v(80, 0) * mm, "construction": true});
            skLineSegment(sketch, "E86", {"start": v(15, 120) * mm, "end": v(15, 108) * mm});
            skLineSegment(sketch, "E87", {"start": v(15, 108) * mm, "end": v(33, 90) * mm});
            skLineSegment(sketch, "E88.MirrorCS", {"start": v(-15, -108) * mm, "end": v(-33, -90) * mm});
            skLineSegment(sketch, "E89.MirrorCS", {"start": v(-15, -120) * mm, "end": v(-15, -108) * mm});
            skArc(sketch, "E90.MirrorCS", {"start": v(15, -120) * mm, "mid": v(0, -135) * mm, "end": v(-15, -120) * mm});
            skCircle(sketch, "E91.MirrorC", {"center": v(0, -120) * mm, "radius": 6 * mm});
            skLineSegment(sketch, "E92.MirrorCS", {"start": v(15, -120) * mm, "end": v(15, -108) * mm});
            skLineSegment(sketch, "E93.MirrorCS", {"start": v(15, -108) * mm, "end": v(33, -90) * mm});
            skLineSegment(sketch, "E94.MirrorCS", {"start": v(0, -90) * mm, "end": v(0, -120) * mm, "construction": true});
            skSolve(sketch);
        }
        {
            var Q0;
            Q0=makeQuery(id+"F16.imprint","IMPRINT",FACE,{"disambiguationData":[TD([[makeQuery(id+"F16.imprint","IMPRINT",EDGE,{"derivedFrom":sQuery(id+"F16.wireOp",EDGE,"E81")}),1.0]])]});
            var Q1;
            {var subQ1=sQuery(id+"F16.wireOp",EDGE,"E79.1");Q1=makeQuery(id+"F16.imprint","IMPRINT",FACE,{"disambiguationData":[TD([[makeQuery(id+"F16.imprint","IMPRINT",EDGE,{"derivedFrom":subQ1}),1.0]])]});}
            var Q2;
            {var subQ0=sQuery(id+"F16.wireOp",EDGE,"E88.MirrorCS");Q2=makeQuery(id+"F16.imprint","IMPRINT",FACE,{"disambiguationData":[TD([[makeQuery(id+"F16.imprint","IMPRINT",EDGE,{"derivedFrom":subQ0}),-1.0]])]});}
            var Q3;
            Q3=makeQuery(id+"F2.opExtrude","CAP_FACE",FACE,{"disambiguationData":[OSD([sQuery(id+"F0.wireOp",EDGE,"E12"),sQuery(id+"F0.wireOp",EDGE,"E13"),sQuery(id+"F0.wireOp",EDGE,"E14"),sQuery(id+"F0.wireOp",EDGE,"E15"),sQuery(id+"F0.wireOp",EDGE,"E17.filletArc"),sQuery(id+"F0.wireOp",EDGE,"E18.filletArc"),sQuery(id+"F0.wireOp",EDGE,"E19.filletArc"),sQuery(id+"F0.wireOp",EDGE,"E20.filletArc"),sQuery(id+"F0.wireOp",EDGE,"E25.0"),sQuery(id+"F0.wireOp",EDGE,"E25.1"),sQuery(id+"F0.wireOp",EDGE,"E25.2"),sQuery(id+"F0.wireOp",EDGE,"E25.3"),sQuery(id+"F0.wireOp",EDGE,"E25.4"),sQuery(id+"F0.wireOp",EDGE,"E25.5"),sQuery(id+"F0.wireOp",EDGE,"E25.6"),sQuery(id+"F0.wireOp",EDGE,"E25.7")])],"isStart":false});
            extrude(context, id + "F17", {"entities" : qUnion([Q0, Q1, Q2]), "endBound" : BoundingType.UP_TO_SURFACE, "endBoundEntityFace" : qUnion([Q3]), "depth" : 25 * mm, "hasDraft" : true, "draftAngle" : 3 * degree});
        }
    });
